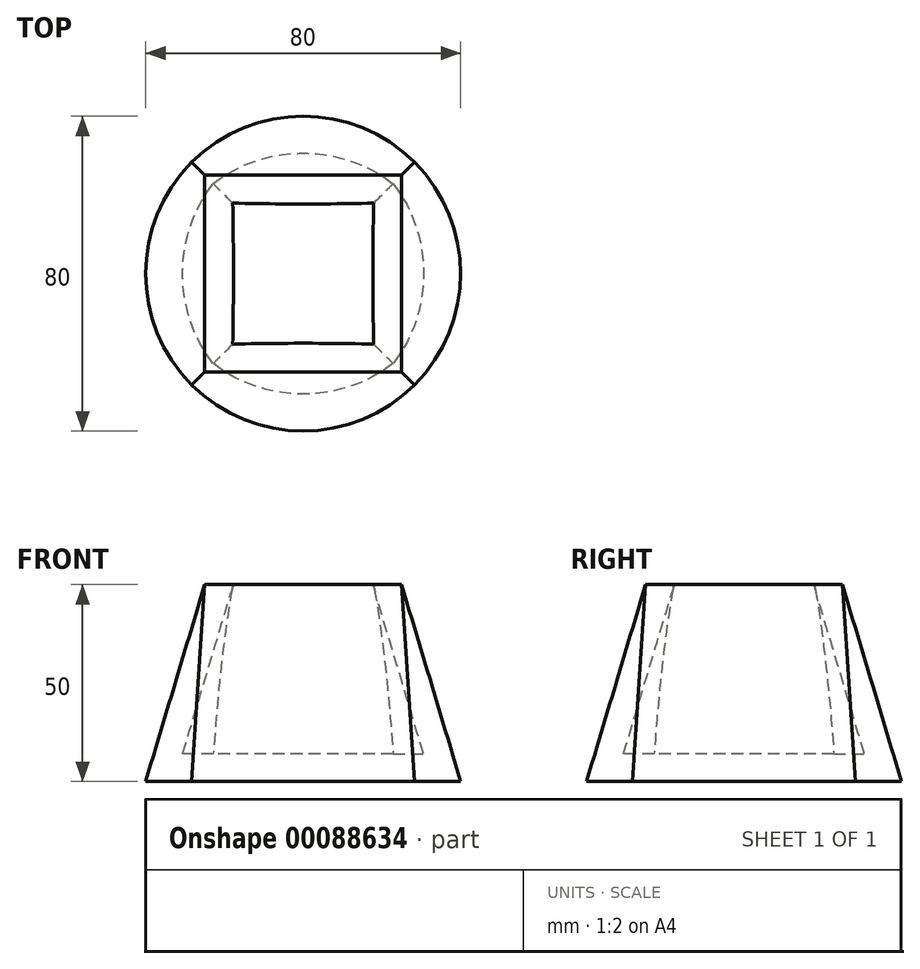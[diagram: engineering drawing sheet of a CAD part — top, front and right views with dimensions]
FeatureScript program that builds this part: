
annotation { "Feature Type Name" : "Feature", "Feature Type Description" : "" }
export const myFeature = defineFeature(function(context is Context, id is Id, definition is map)
    precondition{}
    {
        {
            var Q0;
            Q0=qCreatedBy(makeId("Top.planeOp"),FACE);
            var sketch = newSketch(context, id + "F0", { "sketchPlane" : qUnion([Q0])});
            skCircle(sketch, "E0", {"center": v(0, 0) * mm, "radius": 40 * mm});
            skSolve(sketch);
        }
        {
            var Q0;
            Q0=qCreatedBy(makeId("Top.planeOp"),FACE);
            cPlane(context, id + "F1", {"entities" : qUnion([Q0]), "cplaneType" : CPlaneType.OFFSET, "offset" : 50 * mm, "width" : 152.4 * mm, "height" : 152.4 * mm});
        }
        {
            var Q0;
            Q0=qCreatedBy(id+"F1.planeOp",FACE);
            var sketch = newSketch(context, id + "F2", { "sketchPlane" : qUnion([Q0])});
            skLineSegment(sketch, "E1.bottom", {"start": v(-25, -25) * mm, "end": v(25, -25) * mm});
            skLineSegment(sketch, "E1.top", {"start": v(-25, 25) * mm, "end": v(25, 25) * mm});
            skLineSegment(sketch, "E1.left", {"start": v(-25, -25) * mm, "end": v(-25, 25) * mm});
            skLineSegment(sketch, "E1.right", {"start": v(25, -25) * mm, "end": v(25, 25) * mm});
            skPoint(sketch, "E1.middle", {"position": v(0, 0) * mm});
            skSolve(sketch);
        }
        {
            var Q0;
            Q0=makeQuery(id+"F2.imprint","IMPRINT",FACE,{"disambiguationData":[TD([[makeQuery(id+"F2.imprint","IMPRINT",EDGE,{"derivedFrom":sQuery(id+"F2.wireOp",EDGE,"E1.bottom")}),1.0]])]});
            var Q1;
            Q1=makeQuery(id+"F0.imprint","IMPRINT",FACE,{"disambiguationData":[TD([[makeQuery(id+"F0.imprint","IMPRINT",EDGE,{"derivedFrom":sQuery(id+"F0.wireOp",EDGE,"E0")}),1.0]])]});
            loft(context, id + "F3", {"sheetProfilesArray" : [{ "sheetProfileEntities" : qUnion([Q0]) }, { "sheetProfileEntities" : qUnion([Q1]) }]});
        }
        {
            var Q0;
            Q0=makeQuery(id+"F3.opLoft","CAP_FACE",FACE,{"disambiguationData":[OSD([makeQuery(id+"F2.imprint","IMPRINT",FACE,{"disambiguationData":[TD([[makeQuery(id+"F2.imprint","IMPRINT",EDGE,{"derivedFrom":sQuery(id+"F2.wireOp",EDGE,"E1.bottom")}),1.0]])]})])],"isStart":true});
            shell(context, id + "F4", {"entities" : qUnion([Q0]), "thickness" : 7 * mm});
        }
    });
